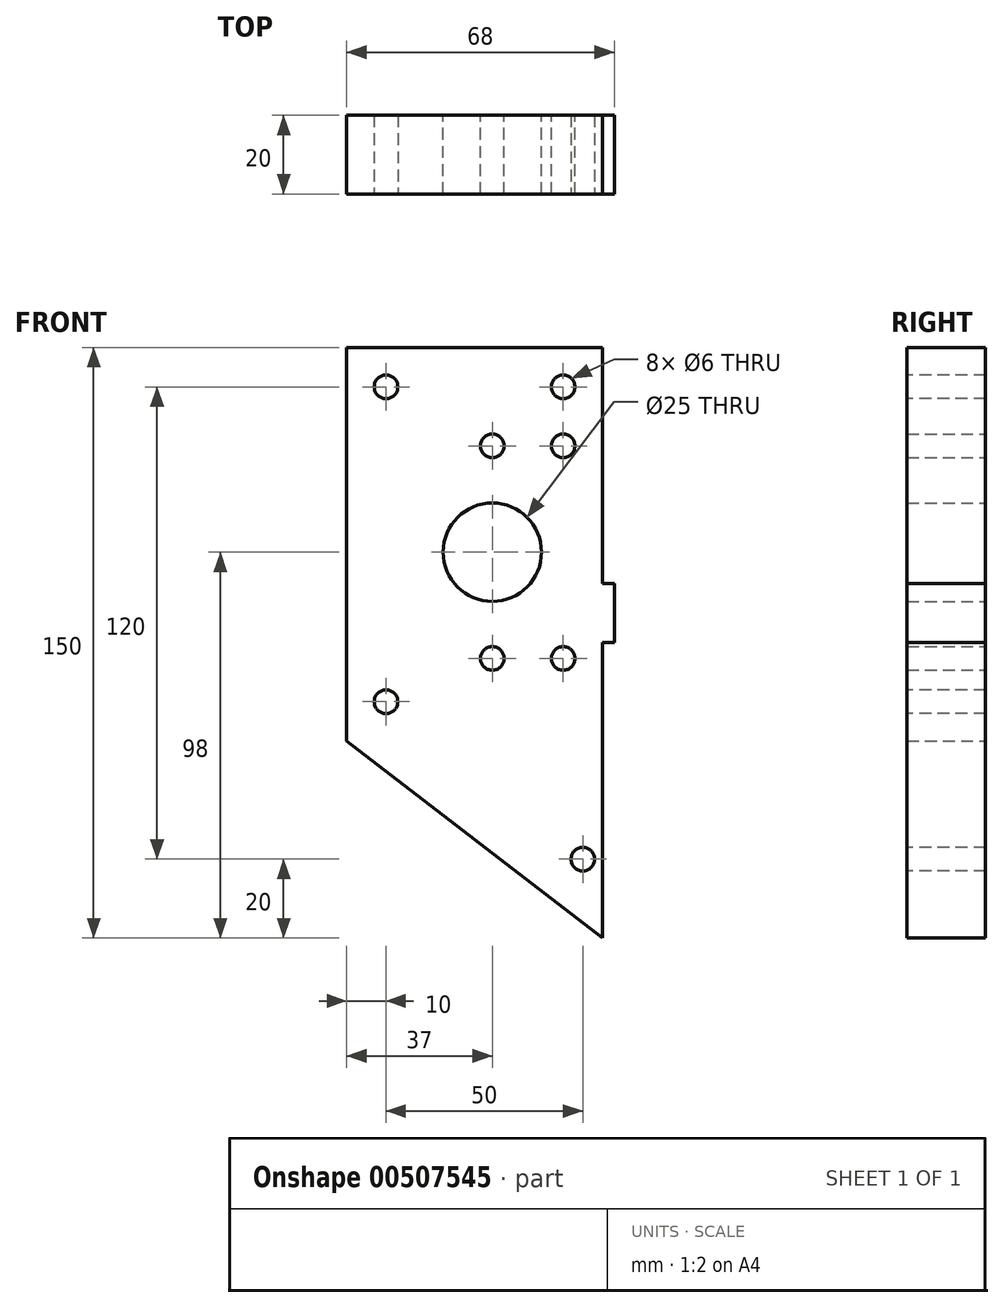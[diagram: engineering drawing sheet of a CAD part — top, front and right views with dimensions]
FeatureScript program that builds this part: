
annotation { "Feature Type Name" : "Feature", "Feature Type Description" : "" }
export const myFeature = defineFeature(function(context is Context, id is Id, definition is map)
    precondition{}
    {
        {
            var Q0;
            Q0=qCreatedBy(makeId("Front.planeOp"),FACE);
            var sketch = newSketch(context, id + "F0", { "sketchPlane" : qUnion([Q0])});
            skLineSegment(sketch, "E0.bottom", {"start": v(60, 0) * mm, "end": v(155, 0) * mm});
            skLineSegment(sketch, "E0.top", {"start": v(-5, 150) * mm, "end": v(155, 150) * mm});
            skLineSegment(sketch, "E0.left", {"start": v(-5, 50) * mm, "end": v(-5, 150) * mm});
            skLineSegment(sketch, "E0.right", {"start": v(155, 0) * mm, "end": v(155, 150) * mm});
            skLineSegment(sketch, "E1.bottom", {"start": v(155, 0) * mm, "end": v(60, 0) * mm});
            skLineSegment(sketch, "E1.top", {"start": v(155, 90) * mm, "end": v(60, 90) * mm});
            skLineSegment(sketch, "E1.left", {"start": v(155, 0) * mm, "end": v(155, 90) * mm});
            skLineSegment(sketch, "E1.right", {"start": v(60, 0) * mm, "end": v(60, 90) * mm});
            skLineSegment(sketch, "E2.bottom", {"start": v(60, 50) * mm, "end": v(-5, 50) * mm});
            skLineSegment(sketch, "E2.top", {"start": v(60, 120) * mm, "end": v(-5, 120) * mm});
            skLineSegment(sketch, "E2.left", {"start": v(60, 50) * mm, "end": v(60, 120) * mm});
            skLineSegment(sketch, "E2.right", {"start": v(-5, 50) * mm, "end": v(-5, 120) * mm});
            skCircle(sketch, "E3", {"center": v(32, 98) * mm, "radius": 18 * mm});
            skLineSegment(sketch, "E4.bottom", {"start": v(1, 75) * mm, "end": v(63, 75) * mm});
            skLineSegment(sketch, "E4.top", {"start": v(1, 119) * mm, "end": v(63, 119) * mm});
            skLineSegment(sketch, "E4.left", {"start": v(1, 75) * mm, "end": v(1, 119) * mm});
            skLineSegment(sketch, "E4.right", {"start": v(63, 75) * mm, "end": v(63, 119) * mm});
            skCircle(sketch, "E5", {"center": v(32, 98) * mm, "radius": 12.5 * mm});
            skLineSegment(sketch, "E6", {"start": v(60, 0) * mm, "end": v(-5, 50) * mm});
            skCircle(sketch, "E7", {"center": v(32, 125) * mm, "radius": 3 * mm});
            skPoint(sketch, "E7.centerSnap0", {"position": v(32, 119) * mm});
            skCircle(sketch, "E8", {"center": v(50, 125) * mm, "radius": 3 * mm});
            skCircle(sketch, "E9", {"center": v(32, 71) * mm, "radius": 3 * mm});
            skCircle(sketch, "E10", {"center": v(50, 71) * mm, "radius": 3 * mm});
            skSolve(sketch);
        }
        {
            var Q0;
            Q0=makeQuery(id+"F0.imprint","IMPRINT",FACE,{"disambiguationData":[TD([[makeQuery(id+"F0.imprint","IMPRINT",EDGE,{"derivedFrom":sQuery(id+"F0.wireOp",EDGE,"E1.bottom")}),-1.0]])]});
            var Q1;
            Q1=makeQuery(id+"F0.imprint","IMPRINT",FACE,{"disambiguationData":[TD([[makeQuery(id+"F0.imprint","IMPRINT",EDGE,{"derivedFrom":sQuery(id+"F0.wireOp",EDGE,"E3")}),-1.0]])]});
            var Q2;
            {var subQ1=sQuery(id+"F0.wireOp",EDGE,"E2.bottom");Q2=makeQuery(id+"F0.imprint","IMPRINT",FACE,{"disambiguationData":[TD([[makeQuery(id+"F0.imprint","IMPRINT",EDGE,{"derivedFrom":subQ1}),-1.0]])]});}
            var Q3;
            Q3=makeQuery(id+"F0.imprint","IMPRINT",FACE,{"disambiguationData":[TD([[makeQuery(id+"F0.imprint","IMPRINT",EDGE,{"derivedFrom":sQuery(id+"F0.wireOp",EDGE,"E0.top")}),-1.0]])]});
            var Q4;
            {var subQ0=sQuery(id+"F0.wireOp",EDGE,"E2.left");var subQ1=sQuery(id+"F0.wireOp",EDGE,"E1.top");var subQ2=makeQuery(id+"F0.imprint","INTERSECT",VERTEX,{"derivedFrom":[subQ1,subQ0]});Q4=makeQuery(id+"F0.imprint","IMPRINT",FACE,{"disambiguationData":[TD([[makeQuery(id+"F0.imprint","IMPRINT",EDGE,{"disambiguationData":[TD([[subQ2,1.0]])],"derivedFrom":subQ1}),-1.0]])]});}
            var Q5;
            {var subQ0=sQuery(id+"F0.wireOp",EDGE,"E2.left");var subQ1=sQuery(id+"F0.wireOp",EDGE,"E1.top");var subQ2=makeQuery(id+"F0.imprint","INTERSECT",VERTEX,{"derivedFrom":[subQ1,subQ0]});Q5=makeQuery(id+"F0.imprint","IMPRINT",FACE,{"disambiguationData":[TD([[makeQuery(id+"F0.imprint","IMPRINT",EDGE,{"disambiguationData":[TD([[subQ2,1.0]])],"derivedFrom":subQ1}),1.0]])]});}
            var Q6;
            Q6=makeQuery(id+"F0.imprint","IMPRINT",FACE,{"disambiguationData":[TD([[makeQuery(id+"F0.imprint","IMPRINT",EDGE,{"derivedFrom":sQuery(id+"F0.wireOp",EDGE,"E5")}),1.0]])]});
            var Q7;
            Q7=makeQuery(id+"F0.imprint","IMPRINT",FACE,{"disambiguationData":[TD([[makeQuery(id+"F0.imprint","IMPRINT",EDGE,{"derivedFrom":sQuery(id+"F0.wireOp",EDGE,"E3")}),1.0]])]});
            var Q8;
            Q8=makeQuery(id+"F0.imprint","IMPRINT",FACE,{"disambiguationData":[TD([[makeQuery(id+"F0.imprint","IMPRINT",EDGE,{"derivedFrom":sQuery(id+"F0.wireOp",EDGE,"E1.right")}),1.0]])]});
            extrude(context, id + "F1", {"entities" : qUnion([Q0, Q1, Q2, Q3, Q4, Q5, Q6, Q7, Q8]), "depth" : 20 * mm, "offsetDistance" : 25 * mm});
        }
        {
            var Q0;
            Q0=makeQuery(id+"F0.imprint","IMPRINT",FACE,{"disambiguationData":[TD([[makeQuery(id+"F0.imprint","IMPRINT",EDGE,{"derivedFrom":sQuery(id+"F0.wireOp",EDGE,"E5")}),1.0]])]});
            extrude(context, id + "F2", {"entities" : qUnion([Q0]), "operationType" : NewBodyOperationType.REMOVE, "depth" : 25 * mm, "offsetDistance" : 25 * mm});
        }
        {
            var Q0;
            Q0=makeQuery(id+"F1.opExtrude","CAP_FACE",FACE,{"disambiguationData":[OSD([sQuery(id+"F0.wireOp",EDGE,"E0.top"),sQuery(id+"F0.wireOp",EDGE,"E0.left"),sQuery(id+"F0.wireOp",EDGE,"E0.right"),sQuery(id+"F0.wireOp",EDGE,"E1.bottom"),sQuery(id+"F0.wireOp",EDGE,"E1.left"),sQuery(id+"F0.wireOp",EDGE,"E2.right"),sQuery(id+"F0.wireOp",EDGE,"E6"),sQuery(id+"F0.wireOp",EDGE,"E7"),sQuery(id+"F0.wireOp",EDGE,"E8"),sQuery(id+"F0.wireOp",EDGE,"E9"),sQuery(id+"F0.wireOp",EDGE,"E10")])],"isStart":false});
            var sketch = newSketch(context, id + "F3", { "sketchPlane" : qUnion([Q0])});
            skLineSegment(sketch, "E11.bottom", {"start": v(155, 0) * mm, "end": v(65, 0) * mm});
            skLineSegment(sketch, "E11.top", {"start": v(155, 90) * mm, "end": v(70, 90) * mm});
            skLineSegment(sketch, "E11.left", {"start": v(155, 0) * mm, "end": v(155, 90) * mm});
            skLineSegment(sketch, "E11.right", {"start": v(65, 0) * mm, "end": v(65, 85) * mm});
            skPoint(sketch, "E12.visualSharp", {"position": v(65, 90) * mm});
            skArc(sketch, "E12.filletArc", {"start": v(70, 90) * mm, "mid": v(66.46, 88.54) * mm, "end": v(65, 85) * mm});
            skSolve(sketch);
        }
        {
            var Q0;
            Q0 = qSketchRegion(id + "F3", true);
            extrude(context, id + "F4", {"entities" : qUnion([Q0]), "operationType" : NewBodyOperationType.REMOVE, "oppositeDirection" : true, "depth" : 25 * mm, "offsetDistance" : 25 * mm});
        }
        {
            var Q0;
            Q0=makeQuery(id+"F1.opExtrude","CAP_FACE",FACE,{"disambiguationData":[OSD([sQuery(id+"F0.wireOp",EDGE,"E0.top"),sQuery(id+"F0.wireOp",EDGE,"E0.left"),sQuery(id+"F0.wireOp",EDGE,"E0.right"),sQuery(id+"F0.wireOp",EDGE,"E1.bottom"),sQuery(id+"F0.wireOp",EDGE,"E1.left"),sQuery(id+"F0.wireOp",EDGE,"E2.right"),sQuery(id+"F0.wireOp",EDGE,"E6"),sQuery(id+"F0.wireOp",EDGE,"E7"),sQuery(id+"F0.wireOp",EDGE,"E8"),sQuery(id+"F0.wireOp",EDGE,"E9"),sQuery(id+"F0.wireOp",EDGE,"E10")])],"isStart":true});
            var sketch = newSketch(context, id + "F5", { "sketchPlane" : qUnion([Q0])});
            skLineSegment(sketch, "E13.bottom", {"start": v(-76, 90) * mm, "end": v(-98, 90) * mm});
            skLineSegment(sketch, "E13.top", {"start": v(-76, 109) * mm, "end": v(-98, 109) * mm});
            skLineSegment(sketch, "E13.left", {"start": v(-76, 90) * mm, "end": v(-76, 109) * mm});
            skLineSegment(sketch, "E13.right", {"start": v(-98, 90) * mm, "end": v(-98, 109) * mm});
            skSolve(sketch);
        }
        {
            var Q0;
            Q0 = qSketchRegion(id + "F5", true);
            extrude(context, id + "F6", {"entities" : qUnion([Q0]), "operationType" : NewBodyOperationType.REMOVE, "oppositeDirection" : true, "depth" : 25 * mm, "offsetDistance" : 25 * mm});
        }
        {
            var Q0;
            Q0=makeQuery(id+"F1.opExtrude","CAP_FACE",FACE,{"disambiguationData":[OSD([sQuery(id+"F0.wireOp",EDGE,"E0.top"),sQuery(id+"F0.wireOp",EDGE,"E0.left"),sQuery(id+"F0.wireOp",EDGE,"E0.right"),sQuery(id+"F0.wireOp",EDGE,"E1.bottom"),sQuery(id+"F0.wireOp",EDGE,"E1.left"),sQuery(id+"F0.wireOp",EDGE,"E2.right"),sQuery(id+"F0.wireOp",EDGE,"E6"),sQuery(id+"F0.wireOp",EDGE,"E7"),sQuery(id+"F0.wireOp",EDGE,"E8"),sQuery(id+"F0.wireOp",EDGE,"E9"),sQuery(id+"F0.wireOp",EDGE,"E10")])],"isStart":false});
            var sketch = newSketch(context, id + "F7", { "sketchPlane" : qUnion([Q0])});
            skLineSegment(sketch, "E14", {"start": v(60, 150) * mm, "end": v(60, 90) * mm});
            skLineSegment(sketch, "E15", {"start": v(65, 85) * mm, "end": v(65, 90) * mm});
            skLineSegment(sketch, "E16", {"start": v(65, 90) * mm, "end": v(60, 90) * mm});
            skSolve(sketch);
        }
        {
            var Q0;
            {var subQ12=sQuery(id+"F7.wireOp",EDGE,"E14");Q0=makeQuery(id+"F7.imprint","IMPRINT",FACE,{"disambiguationData":[TD([[makeQuery(id+"F7.imprint","IMPRINT",EDGE,{"derivedFrom":subQ12}),1.0]])]});}
            extrude(context, id + "F8", {"entities" : qUnion([Q0]), "operationType" : NewBodyOperationType.REMOVE, "oppositeDirection" : true, "depth" : 25 * mm, "offsetDistance" : 25 * mm});
        }
        {
            var Q0;
            Q0=makeQuery(id+"F1.opExtrude","CAP_FACE",FACE,{"disambiguationData":[OSD([sQuery(id+"F0.wireOp",EDGE,"E0.top"),sQuery(id+"F0.wireOp",EDGE,"E0.left"),sQuery(id+"F0.wireOp",EDGE,"E0.right"),sQuery(id+"F0.wireOp",EDGE,"E1.bottom"),sQuery(id+"F0.wireOp",EDGE,"E1.left"),sQuery(id+"F0.wireOp",EDGE,"E2.right"),sQuery(id+"F0.wireOp",EDGE,"E6"),sQuery(id+"F0.wireOp",EDGE,"E7"),sQuery(id+"F0.wireOp",EDGE,"E8"),sQuery(id+"F0.wireOp",EDGE,"E9"),sQuery(id+"F0.wireOp",EDGE,"E10")])],"isStart":false});
            var sketch = newSketch(context, id + "F9", { "sketchPlane" : qUnion([Q0])});
            skCircle(sketch, "E17", {"center": v(5, 140) * mm, "radius": 3 * mm});
            skCircle(sketch, "E18", {"center": v(50, 140) * mm, "radius": 3 * mm});
            skCircle(sketch, "E19", {"center": v(5, 60) * mm, "radius": 3 * mm});
            skCircle(sketch, "E20", {"center": v(55, 20) * mm, "radius": 3 * mm});
            skSolve(sketch);
        }
        {
            var Q0;
            Q0 = qSketchRegion(id + "F9", true);
            extrude(context, id + "F10", {"entities" : qUnion([Q0]), "operationType" : NewBodyOperationType.REMOVE, "oppositeDirection" : true, "depth" : 25 * mm, "offsetDistance" : 25 * mm});
        }
    });
